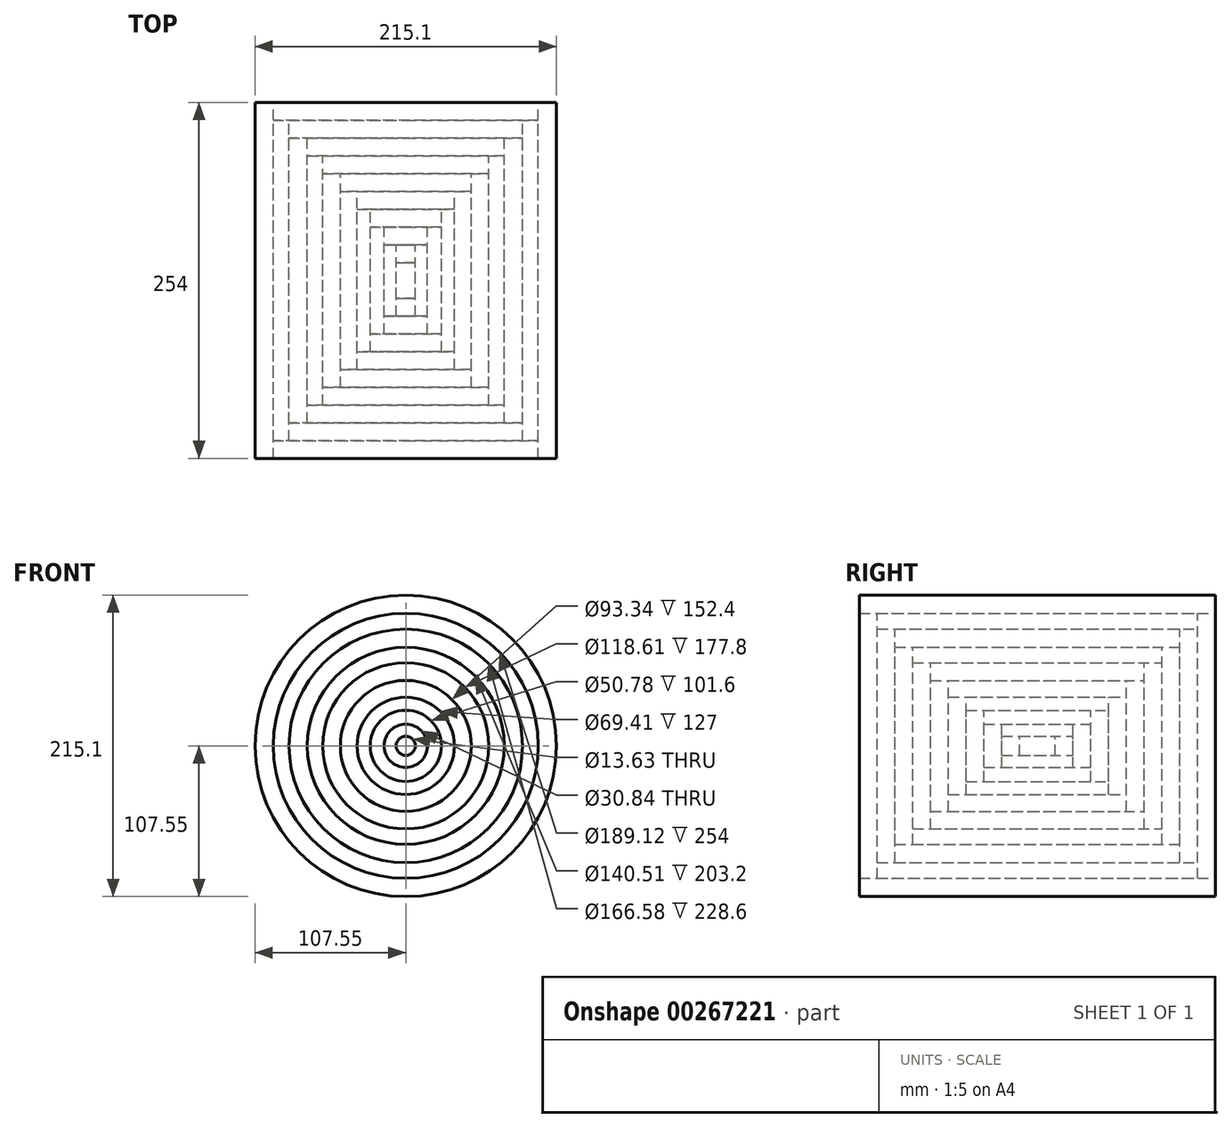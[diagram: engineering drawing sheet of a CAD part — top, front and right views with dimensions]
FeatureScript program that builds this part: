
annotation { "Feature Type Name" : "Feature", "Feature Type Description" : "" }
export const myFeature = defineFeature(function(context is Context, id is Id, definition is map)
    precondition{}
    {
        {
            var Q0;
            Q0=qCreatedBy(makeId("Front.planeOp"),FACE);
            var sketch = newSketch(context, id + "F0", { "sketchPlane" : qUnion([Q0])});
            skCircle(sketch, "E0", {"center": v(0, 0) * mm, "radius": 107.55 * mm});
            skCircle(sketch, "E1", {"center": v(0, 0) * mm, "radius": 94.56 * mm});
            skCircle(sketch, "E2", {"center": v(0, 0) * mm, "radius": 83.29 * mm});
            skCircle(sketch, "E3", {"center": v(0, 0) * mm, "radius": 70.25 * mm});
            skCircle(sketch, "E4", {"center": v(0, 0) * mm, "radius": 59.3 * mm});
            skCircle(sketch, "E5", {"center": v(0, 0) * mm, "radius": 46.67 * mm});
            skCircle(sketch, "E6", {"center": v(0, 0) * mm, "radius": 34.7 * mm});
            skCircle(sketch, "E7", {"center": v(0, 0) * mm, "radius": 25.39 * mm});
            skCircle(sketch, "E8", {"center": v(0, 0) * mm, "radius": 15.42 * mm});
            skCircle(sketch, "E9", {"center": v(0, 0) * mm, "radius": 6.81 * mm});
            skSolve(sketch);
        }
        {
            var Q0;
            Q0=makeQuery(id+"F0.imprint","IMPRINT",FACE,{"disambiguationData":[TD([[makeQuery(id+"F0.imprint","IMPRINT",EDGE,{"derivedFrom":sQuery(id+"F0.wireOp",EDGE,"E9")}),1.0]])]});
            extrude(context, id + "F1", {"entities" : qUnion([Q0]), "endBound" : BoundingType.SYMMETRIC, "depth" : 25.4 * mm});
        }
        {
            var Q0;
            Q0=makeQuery(id+"F0.imprint","IMPRINT",FACE,{"disambiguationData":[TD([[makeQuery(id+"F0.imprint","IMPRINT",EDGE,{"derivedFrom":sQuery(id+"F0.wireOp",EDGE,"E8")}),1.0]])]});
            extrude(context, id + "F2", {"entities" : qUnion([Q0]), "endBound" : BoundingType.SYMMETRIC, "depth" : 50.8 * mm});
        }
        {
            var Q0;
            Q0=makeQuery(id+"F0.imprint","IMPRINT",FACE,{"disambiguationData":[TD([[makeQuery(id+"F0.imprint","IMPRINT",EDGE,{"derivedFrom":sQuery(id+"F0.wireOp",EDGE,"E7")}),1.0]])]});
            extrude(context, id + "F3", {"entities" : qUnion([Q0]), "endBound" : BoundingType.SYMMETRIC, "depth" : 76.2 * mm});
        }
        {
            var Q0;
            Q0=makeQuery(id+"F0.imprint","IMPRINT",FACE,{"disambiguationData":[TD([[makeQuery(id+"F0.imprint","IMPRINT",EDGE,{"derivedFrom":sQuery(id+"F0.wireOp",EDGE,"E6")}),1.0]])]});
            extrude(context, id + "F4", {"entities" : qUnion([Q0]), "endBound" : BoundingType.SYMMETRIC, "depth" : 101.6 * mm});
        }
        {
            var Q0;
            Q0=makeQuery(id+"F0.imprint","IMPRINT",FACE,{"disambiguationData":[TD([[makeQuery(id+"F0.imprint","IMPRINT",EDGE,{"derivedFrom":sQuery(id+"F0.wireOp",EDGE,"E5")}),1.0]])]});
            extrude(context, id + "F5", {"entities" : qUnion([Q0]), "endBound" : BoundingType.SYMMETRIC, "depth" : 127 * mm});
        }
        {
            var Q0;
            Q0=makeQuery(id+"F0.imprint","IMPRINT",FACE,{"disambiguationData":[TD([[makeQuery(id+"F0.imprint","IMPRINT",EDGE,{"derivedFrom":sQuery(id+"F0.wireOp",EDGE,"E4")}),1.0]])]});
            extrude(context, id + "F6", {"entities" : qUnion([Q0]), "endBound" : BoundingType.SYMMETRIC, "depth" : 152.4 * mm});
        }
        {
            var Q0;
            Q0=makeQuery(id+"F0.imprint","IMPRINT",FACE,{"disambiguationData":[TD([[makeQuery(id+"F0.imprint","IMPRINT",EDGE,{"derivedFrom":sQuery(id+"F0.wireOp",EDGE,"E3")}),1.0]])]});
            extrude(context, id + "F7", {"entities" : qUnion([Q0]), "endBound" : BoundingType.SYMMETRIC, "depth" : 177.8 * mm});
        }
        {
            var Q0;
            Q0=makeQuery(id+"F0.imprint","IMPRINT",FACE,{"disambiguationData":[TD([[makeQuery(id+"F0.imprint","IMPRINT",EDGE,{"derivedFrom":sQuery(id+"F0.wireOp",EDGE,"E2")}),1.0]])]});
            extrude(context, id + "F8", {"entities" : qUnion([Q0]), "endBound" : BoundingType.SYMMETRIC, "depth" : 203.2 * mm});
        }
        {
            var Q0;
            Q0=makeQuery(id+"F0.imprint","IMPRINT",FACE,{"disambiguationData":[TD([[makeQuery(id+"F0.imprint","IMPRINT",EDGE,{"derivedFrom":sQuery(id+"F0.wireOp",EDGE,"E1")}),1.0]])]});
            extrude(context, id + "F9", {"entities" : qUnion([Q0]), "endBound" : BoundingType.SYMMETRIC, "depth" : 228.6 * mm});
        }
        {
            var Q0;
            Q0=makeQuery(id+"F0.imprint","IMPRINT",FACE,{"disambiguationData":[TD([[makeQuery(id+"F0.imprint","IMPRINT",EDGE,{"derivedFrom":sQuery(id+"F0.wireOp",EDGE,"E0")}),1.0]])]});
            extrude(context, id + "F10", {"entities" : qUnion([Q0]), "endBound" : BoundingType.SYMMETRIC, "depth" : 254 * mm});
        }
    });
